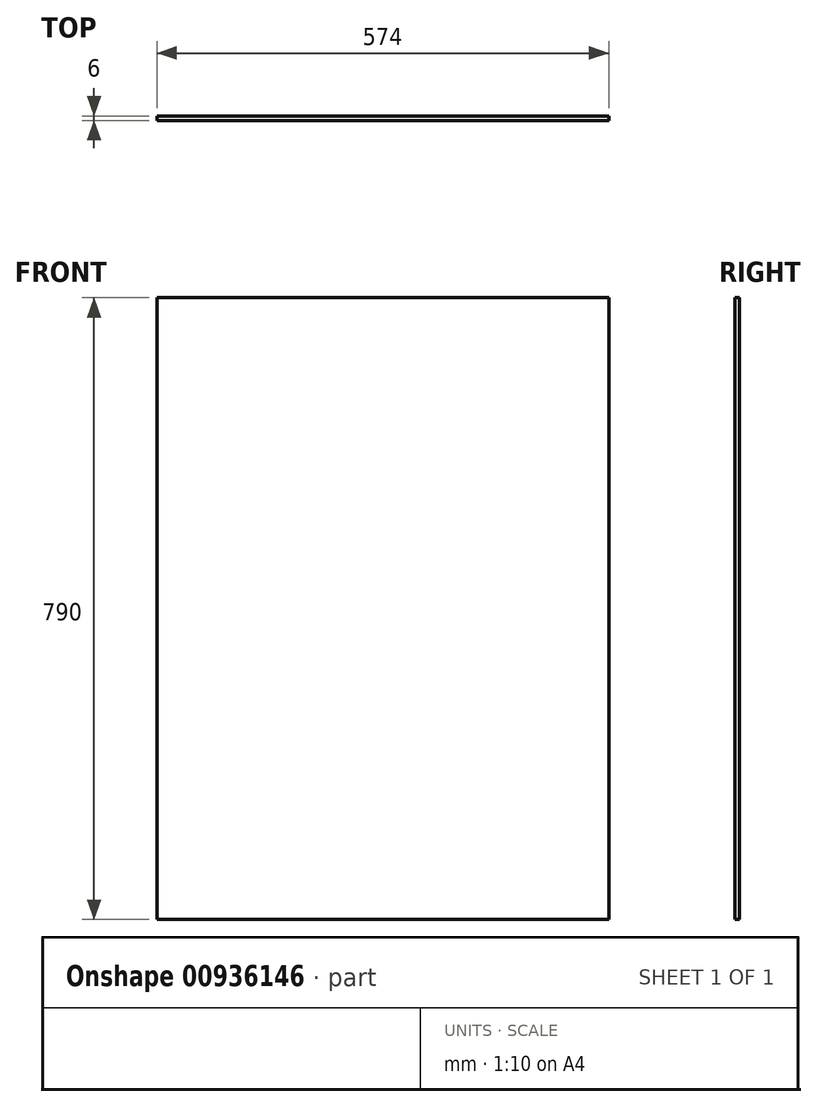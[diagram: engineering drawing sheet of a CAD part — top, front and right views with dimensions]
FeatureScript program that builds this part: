
annotation { "Feature Type Name" : "Feature", "Feature Type Description" : "" }
export const myFeature = defineFeature(function(context is Context, id is Id, definition is map)
    precondition{}
    {
        {
            var Q0;
            Q0=qCreatedBy(makeId("Front.planeOp"),FACE);
            var sketch = newSketch(context, id + "F0", { "sketchPlane" : qUnion([Q0])});
            skLineSegment(sketch, "E0.bottom", {"start": v(0, 0) * mm, "end": v(574, 0) * mm});
            skLineSegment(sketch, "E0.top", {"start": v(0, 790) * mm, "end": v(574, 790) * mm});
            skLineSegment(sketch, "E0.left", {"start": v(0, 0) * mm, "end": v(0, 790) * mm});
            skLineSegment(sketch, "E0.right", {"start": v(574, 0) * mm, "end": v(574, 790) * mm});
            skSolve(sketch);
        }
        {
            var Q0;
            Q0=makeQuery(id+"F0.imprint","IMPRINT",FACE,{"disambiguationData":[TD([[makeQuery(id+"F0.imprint","IMPRINT",EDGE,{"derivedFrom":sQuery(id+"F0.wireOp",EDGE,"E0.bottom")}),1.0]])]});
            extrude(context, id + "F1", {"entities" : qUnion([Q0]), "depth" : 6 * mm, "offsetDistance" : 25 * mm});
        }
    });
